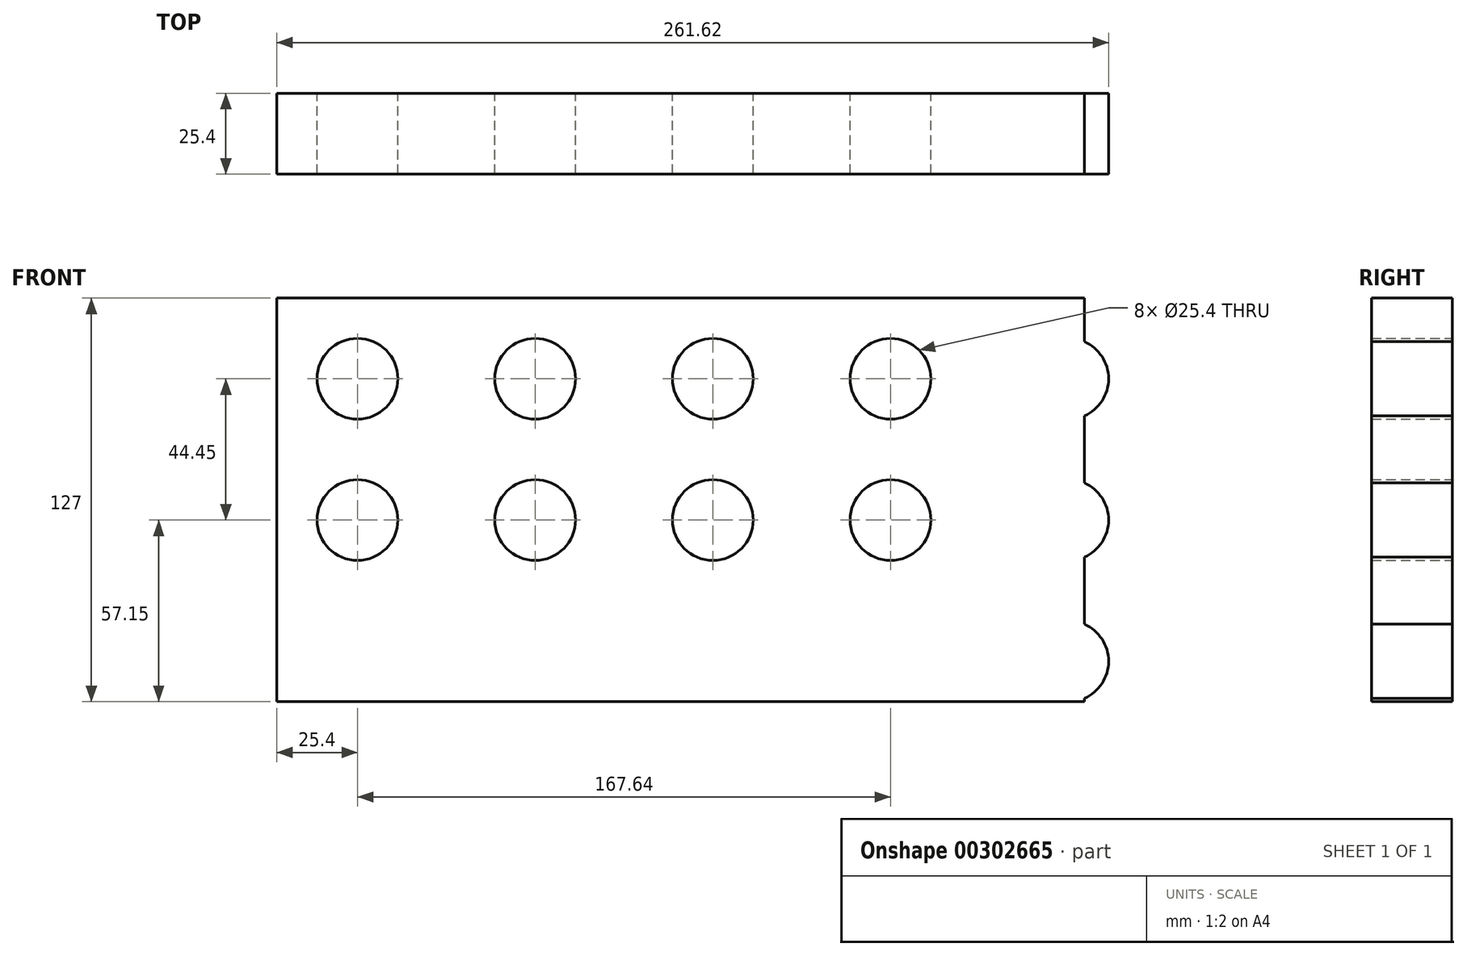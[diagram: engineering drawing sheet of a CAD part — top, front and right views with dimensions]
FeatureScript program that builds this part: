
annotation { "Feature Type Name" : "Feature", "Feature Type Description" : "" }
export const myFeature = defineFeature(function(context is Context, id is Id, definition is map)
    precondition{}
    {
        {
            var Q0;
            Q0=qCreatedBy(makeId("Front.planeOp"),FACE);
            var sketch = newSketch(context, id + "F0", { "sketchPlane" : qUnion([Q0])});
            skLineSegment(sketch, "E0.bottom", {"start": v(0, 0) * mm, "end": v(254, 0) * mm});
            skLineSegment(sketch, "E0.top", {"start": v(0, -127) * mm, "end": v(254, -127) * mm});
            skLineSegment(sketch, "E0.left", {"start": v(0, 0) * mm, "end": v(0, -127) * mm});
            skLineSegment(sketch, "E0.right", {"start": v(254, 0) * mm, "end": v(254, -127) * mm});
            skCircle(sketch, "E1", {"center": v(25.4, -25.4) * mm, "radius": 12.7 * mm});
            skCircle(sketch, "E2.0.1.0", {"center": v(25.4, -69.85) * mm, "radius": 12.7 * mm});
            skCircle(sketch, "E2.0.2.0", {"center": v(25.4, -114.3) * mm, "radius": 12.7 * mm});
            skCircle(sketch, "E2.1.0.0", {"center": v(81.28, -25.4) * mm, "radius": 12.7 * mm});
            skCircle(sketch, "E2.1.1.0", {"center": v(81.28, -69.85) * mm, "radius": 12.7 * mm});
            skCircle(sketch, "E2.1.2.0", {"center": v(81.28, -114.3) * mm, "radius": 12.7 * mm});
            skCircle(sketch, "E2.2.0.0", {"center": v(137.16, -25.4) * mm, "radius": 12.7 * mm});
            skCircle(sketch, "E2.2.1.0", {"center": v(137.16, -69.85) * mm, "radius": 12.7 * mm});
            skCircle(sketch, "E2.2.2.0", {"center": v(137.16, -114.3) * mm, "radius": 12.7 * mm});
            skCircle(sketch, "E2.3.0.0", {"center": v(193.04, -25.4) * mm, "radius": 12.7 * mm});
            skCircle(sketch, "E2.3.1.0", {"center": v(193.04, -69.85) * mm, "radius": 12.7 * mm});
            skCircle(sketch, "E2.3.2.0", {"center": v(193.04, -114.3) * mm, "radius": 12.7 * mm});
            skCircle(sketch, "E2.4.0.0", {"center": v(248.92, -25.4) * mm, "radius": 12.7 * mm});
            skCircle(sketch, "E2.4.1.0", {"center": v(248.92, -69.85) * mm, "radius": 12.7 * mm});
            skCircle(sketch, "E2.4.2.0", {"center": v(248.92, -114.3) * mm, "radius": 12.7 * mm});
            skLineSegment(sketch, "E2.direction1", {"start": v(25.4, -25.4) * mm, "end": v(81.28, -25.4) * mm, "construction": true});
            skLineSegment(sketch, "E2.direction2", {"start": v(25.4, -25.4) * mm, "end": v(25.4, -69.85) * mm, "construction": true});
            skSolve(sketch);
        }
        {
            var Q0;
            Q0 = qSketchRegion(id + "F0", true);
            extrude(context, id + "F1", {"entities" : qUnion([Q0]), "depth" : 25.4 * mm});
        }
    });
